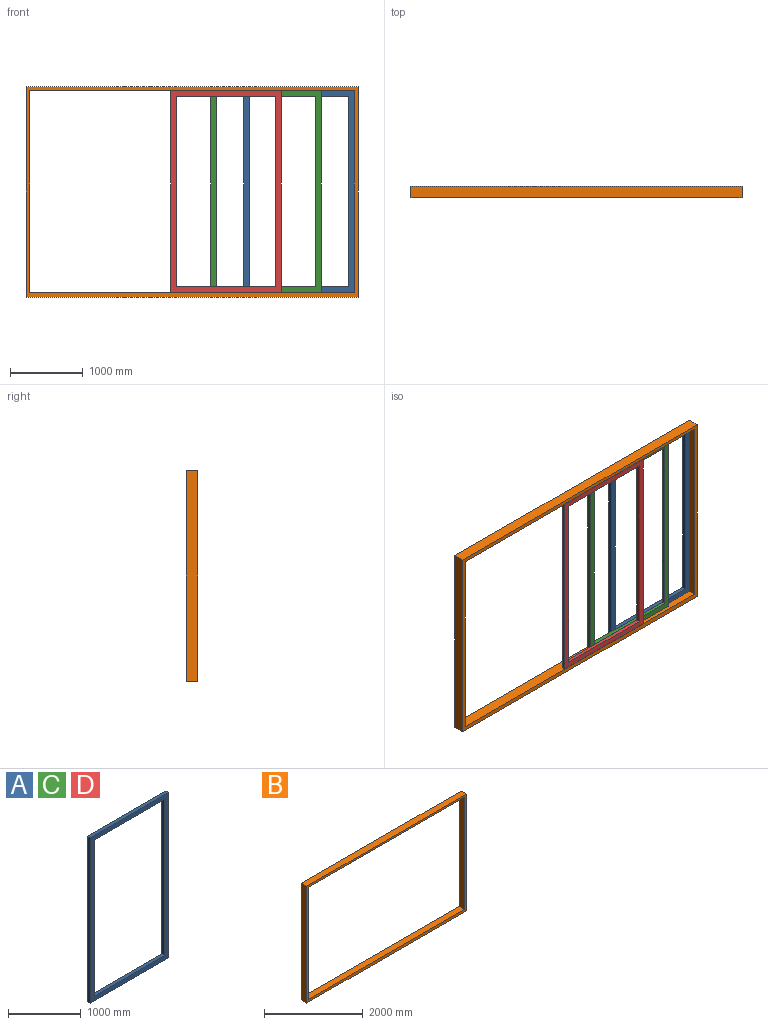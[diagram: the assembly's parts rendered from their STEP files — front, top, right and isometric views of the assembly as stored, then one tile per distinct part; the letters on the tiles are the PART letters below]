
ASSEMBLY  parts=4 mates=4
PART A: 10 faces, bbox 1524x50.8x2781.3 mm
  f0: plane 1524x50.8mm, normal (0,0,1), area 77419.2mm2, adj f1,f3,f4,f5
  f1: plane 2781.3x50.8mm, normal (-1,0,0), area 141290mm2, adj f0,f2,f4,f5
  f2: plane 1524x50.8mm, normal (0,0,-1), area 77419.2mm2, adj f1,f3,f4,f5
  f3: plane 2781.3x50.8mm, normal (1,0,0), area 141290mm2, adj f0,f2,f4,f5
  f4: plane 2781.3x1524mm, normal (0,-1,0), area 632902mm2, adj f0,f1,f2,f3,f6,f7,f8,f9
  f5: plane 2781.3x1524mm, normal (0,1,0), area 632902mm2, adj f0,f1,f2,f3,f6,f7,f8,f9
  f6: plane 2628.9x50.8mm, normal (1,0,0), area 133548.1mm2, adj f4,f5,f7,f9
  f7: plane 1371.6x50.8mm, normal (0,0,1), area 69677.3mm2, adj f4,f5,f6,f8
  f8: plane 2628.9x50.8mm, normal (-1,0,0), area 133548.1mm2, adj f4,f5,f7,f9
  f9: plane 1371.6x50.8mm, normal (0,0,-1), area 69677.3mm2, adj f4,f5,f6,f8
PART B: 10 faces, bbox 4572x152.4x2895.6 mm
  f0: plane 4572x152.4mm, normal (0,0,1), area 696772.8mm2, adj f1,f3,f4,f5
  f1: plane 2895.6x152.4mm, normal (-1,0,0), area 441289.4mm2, adj f0,f2,f4,f5
  f2: plane 4572x152.4mm, normal (0,0,-1), area 696772.8mm2, adj f1,f3,f4,f5
  f3: plane 2895.6x152.4mm, normal (1,0,0), area 441289.4mm2, adj f0,f2,f4,f5
  f4: plane 4572x2895.6mm, normal (0,-1,0), area 805159.7mm2, adj f0,f1,f2,f3,f6,f7,f8,f9
  f5: plane 4572x2895.6mm, normal (0,1,0), area 805159.7mm2, adj f0,f1,f2,f3,f6,f7,f8,f9
  f6: plane 2781.3x152.4mm, normal (1,0,0), area 423870.1mm2, adj f4,f5,f7,f9
  f7: plane 4470.4x152.4mm, normal (0,0,1), area 681289mm2, adj f4,f5,f6,f8
  f8: plane 2781.3x152.4mm, normal (-1,0,0), area 423870.1mm2, adj f4,f5,f7,f9
  f9: plane 4470.4x152.4mm, normal (0,0,-1), area 681289mm2, adj f4,f5,f6,f8
PART C: same geometry as A
PART D: same geometry as A
PLACE A t=(1473.2,0,6.35)mm
PLACE B at identity fixed
PLACE C t=(1020.05,-50.8,6.35)mm
PLACE D t=(468.64,-101.6,6.35)mm
MATE slider D.f1 <-> B.f6  axis (1,0,0) through (-293.36,-152.4,1397)mm
MATE fastened A.f3 <-> B.f8  axis (1,0,0) through (2235.2,0,1397)mm
MATE planar D.f0 <-> B.f9  axis (0,0,1) through (468.64,-127,1397)mm
MATE slider C.f3 <-> A.f1  axis (1,0,0) through (1782.05,-50.8,1397)mm
